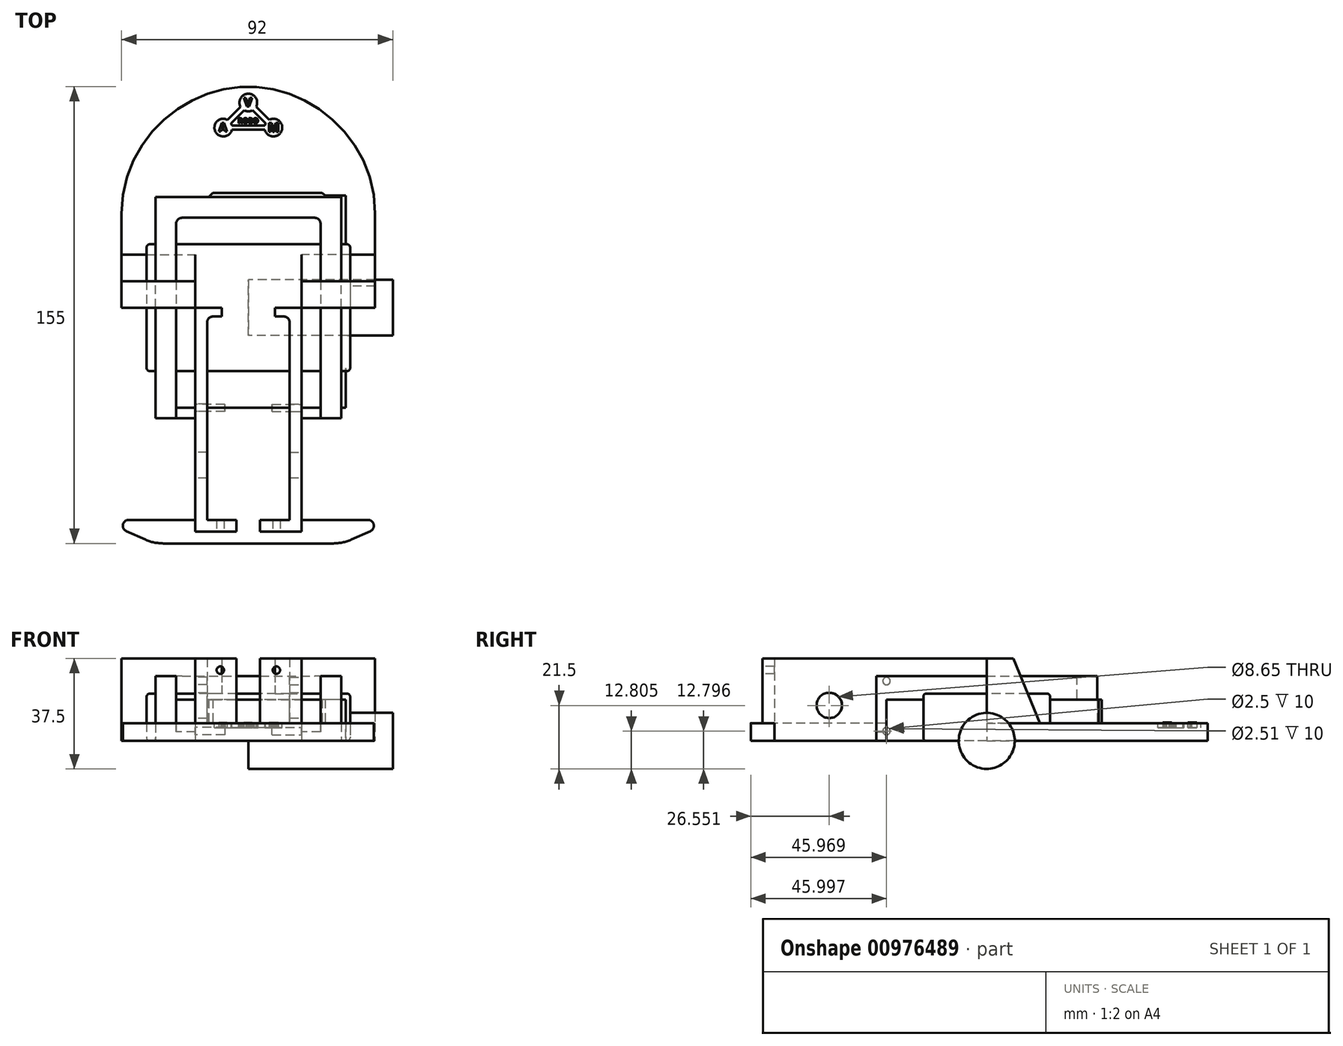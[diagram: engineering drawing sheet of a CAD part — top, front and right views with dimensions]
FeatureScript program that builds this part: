
annotation { "Feature Type Name" : "Feature", "Feature Type Description" : "" }
export const myFeature = defineFeature(function(context is Context, id is Id, definition is map)
    precondition{}
    {
        {
            var Q0;
            Q0=qCreatedBy(makeId("Top.planeOp"),FACE);
            var sketch = newSketch(context, id + "F0", { "sketchPlane" : qUnion([Q0])});
            skLineSegment(sketch, "E0.bottom", {"start": v(34.5, 21.5) * mm, "end": v(-34.5, 21.5) * mm});
            skLineSegment(sketch, "E0.top", {"start": v(34.5, -21.5) * mm, "end": v(-34.5, -21.5) * mm});
            skLineSegment(sketch, "E0.left", {"start": v(34.5, 21.5) * mm, "end": v(34.5, -21.5) * mm});
            skLineSegment(sketch, "E0.right", {"start": v(-34.5, 21.5) * mm, "end": v(-34.5, -21.5) * mm});
            skPoint(sketch, "E0.middle", {"position": v(0, 0) * mm});
            skSolve(sketch);
        }
        {
            var Q0;
            Q0 = qSketchRegion(id + "F0", true);
            extrude(context, id + "F1", {"entities" : qUnion([Q0]), "depth" : 16 * mm, "offsetDistance" : 25 * mm});
        }
        {
            var Q0;
            Q0=makeQuery(id+"F1.opExtrude","SWEPT_EDGE",EDGE,{"disambiguationData":[OSD([sQuery(id+"F0.wireOp",EDGE,"E0.bottom"),sQuery(id+"F0.wireOp",EDGE,"E0.right")])]});
            var Q1;
            Q1=makeQuery(id+"F1.opExtrude","SWEPT_EDGE",EDGE,{"disambiguationData":[OSD([sQuery(id+"F0.wireOp",EDGE,"E0.top"),sQuery(id+"F0.wireOp",EDGE,"E0.left")])]});
            var Q2;
            Q2=makeQuery(id+"F1.opExtrude","SWEPT_EDGE",EDGE,{"disambiguationData":[OSD([sQuery(id+"F0.wireOp",EDGE,"E0.top"),sQuery(id+"F0.wireOp",EDGE,"E0.right")])]});
            var Q3;
            Q3=makeQuery(id+"F1.opExtrude","CAP_EDGE",EDGE,{"disambiguationData":[OSD([sQuery(id+"F0.wireOp",EDGE,"E0.top")])],"isStart":true});
            var Q4;
            Q4=makeQuery(id+"F1.opExtrude","CAP_EDGE",EDGE,{"disambiguationData":[OSD([sQuery(id+"F0.wireOp",EDGE,"E0.left")])],"isStart":false});
            var Q5;
            Q5=makeQuery(id+"F1.opExtrude","CAP_EDGE",EDGE,{"disambiguationData":[OSD([sQuery(id+"F0.wireOp",EDGE,"E0.right")])],"isStart":true});
            var Q6;
            Q6=makeQuery(id+"F1.opExtrude","CAP_EDGE",EDGE,{"disambiguationData":[OSD([sQuery(id+"F0.wireOp",EDGE,"E0.right")])],"isStart":false});
            var Q7;
            Q7=makeQuery(id+"F1.opExtrude","SWEPT_EDGE",EDGE,{"disambiguationData":[OSD([sQuery(id+"F0.wireOp",EDGE,"E0.bottom"),sQuery(id+"F0.wireOp",EDGE,"E0.left")])]});
            var Q8;
            Q8=makeQuery(id+"F1.opExtrude","CAP_EDGE",EDGE,{"disambiguationData":[OSD([sQuery(id+"F0.wireOp",EDGE,"E0.bottom")])],"isStart":true});
            var Q9;
            Q9=makeQuery(id+"F1.opExtrude","CAP_EDGE",EDGE,{"disambiguationData":[OSD([sQuery(id+"F0.wireOp",EDGE,"E0.bottom")])],"isStart":false});
            var Q10;
            Q10=makeQuery(id+"F1.opExtrude","CAP_EDGE",EDGE,{"disambiguationData":[OSD([sQuery(id+"F0.wireOp",EDGE,"E0.top")])],"isStart":false});
            var Q11;
            Q11=makeQuery(id+"F1.opExtrude","CAP_EDGE",EDGE,{"disambiguationData":[OSD([sQuery(id+"F0.wireOp",EDGE,"E0.left")])],"isStart":true});
            fillet(context, id + "F2", {"entities" : qUnion([Q0, Q1, Q2, Q3, Q4, Q5, Q6, Q7, Q8, Q9, Q10, Q11]), "radius" : 1 * mm, "tangentPropagation" : true, "allowEdgeOverflow" : false});
        }
        {
            var Q0;
            Q0=qCreatedBy(makeId("Right.planeOp"),FACE);
            var sketch = newSketch(context, id + "F3", { "sketchPlane" : qUnion([Q0])});
            skCircle(sketch, "E1", {"center": v(0, 0) * mm, "radius": 9.5 * mm});
            skSolve(sketch);
        }
        {
            var Q0;
            Q0 = qSketchRegion(id + "F3", true);
            extrude(context, id + "F4", {"entities" : qUnion([Q0]), "depth" : 49 * mm, "offsetDistance" : 25 * mm});
        }
        {
            var Q0;
            Q0=qCreatedBy(makeId("Top.planeOp"),FACE);
            var sketch = newSketch(context, id + "F5", { "sketchPlane" : qUnion([Q0])});
            skLineSegment(sketch, "E2", {"start": v(33, 38) * mm, "end": v(33, -34) * mm});
            skLineSegment(sketch, "E3", {"start": v(33, -34) * mm, "end": v(-30, -34) * mm});
            skLineSegment(sketch, "E4", {"start": v(-30, -34) * mm, "end": v(-30, 34) * mm});
            skLineSegment(sketch, "E5", {"start": v(-30, 34) * mm, "end": v(-27.12, 36.88) * mm});
            skLineSegment(sketch, "E6", {"start": v(-27.12, 36.88) * mm, "end": v(-14.12, 36.88) * mm});
            skLineSegment(sketch, "E7", {"start": v(-14.12, 36.88) * mm, "end": v(-12, 39) * mm});
            skLineSegment(sketch, "E8", {"start": v(-12, 39) * mm, "end": v(25, 39) * mm});
            skLineSegment(sketch, "E9", {"start": v(33, 38) * mm, "end": v(26, 38) * mm});
            skLineSegment(sketch, "E10", {"start": v(26, 38) * mm, "end": v(25, 39) * mm});
            skLineSegment(sketch, "E11", {"start": v(-30, 0) * mm, "end": v(0, 0) * mm, "construction": true});
            skSolve(sketch);
        }
        {
            var Q0;
            Q0 = qSketchRegion(id + "F5", true);
            extrude(context, id + "F6", {"entities" : qUnion([Q0]), "depth" : 14 * mm, "offsetDistance" : 25 * mm});
        }
        {
            var Q0;
            Q0=qCreatedBy(makeId("Top.planeOp"),FACE);
            var sketch = newSketch(context, id + "F7", { "sketchPlane" : qUnion([Q0])});
            skLineSegment(sketch, "E12", {"start": v(-18, -72) * mm, "end": v(-18, 0) * mm});
            skLineSegment(sketch, "E13", {"start": v(-18, 0) * mm, "end": v(-43, 0) * mm});
            skLineSegment(sketch, "E14", {"start": v(-43, 0) * mm, "end": v(-43, 32) * mm});
            skLineSegment(sketch, "E15", {"start": v(-43, 32) * mm, "end": v(-43, 57) * mm, "construction": true});
            skLineSegment(sketch, "E16", {"start": v(-18, -72) * mm, "end": v(-40.58, -72) * mm});
            skLineSegment(sketch, "E17", {"start": v(0, -80) * mm, "end": v(-28.82, -80) * mm});
            skLineSegment(sketch, "E18", {"start": v(-18, 0) * mm, "end": v(0, 0) * mm, "construction": true});
            skLineSegment(sketch, "E19", {"start": v(0, 0) * mm, "end": v(0, -80) * mm, "construction": true});
            skLineSegment(sketch, "E20", {"start": v(-41.39, -75.83) * mm, "end": v(-34.9, -78.7) * mm});
            skPoint(sketch, "E21.visualSharp", {"position": v(-50, -72) * mm});
            skArc(sketch, "E21.filletArc", {"start": v(-40.58, -72) * mm, "mid": v(-42.53, -73.58) * mm, "end": v(-41.39, -75.83) * mm});
            skLineSegment(sketch, "E22", {"start": v(0, 0) * mm, "end": v(0, 75) * mm, "construction": true});
            skArc(sketch, "E23.MirrorCS", {"start": v(40.58, -72) * mm, "mid": v(42.53, -73.58) * mm, "end": v(41.39, -75.83) * mm});
            skLineSegment(sketch, "E24.MirrorCS", {"start": v(41.39, -75.83) * mm, "end": v(34.9, -78.7) * mm});
            skLineSegment(sketch, "E25.MirrorCS", {"start": v(18, -72) * mm, "end": v(40.58, -72) * mm});
            skLineSegment(sketch, "E26.MirrorCS", {"start": v(18, 0) * mm, "end": v(43, 0) * mm});
            skLineSegment(sketch, "E27.MirrorCS", {"start": v(18, 0) * mm, "end": v(0, 0) * mm, "construction": true});
            skLineSegment(sketch, "E28.MirrorCS", {"start": v(43, 32) * mm, "end": v(43, 57) * mm, "construction": true});
            skLineSegment(sketch, "E29.MirrorCS", {"start": v(0, -80) * mm, "end": v(28.82, -80) * mm});
            skPoint(sketch, "E30.MirrorP", {"position": v(50, -72) * mm});
            skLineSegment(sketch, "E31.MirrorCS", {"start": v(18, -72) * mm, "end": v(18, 0) * mm});
            skLineSegment(sketch, "E32.MirrorCS", {"start": v(43, 0) * mm, "end": v(43, 32) * mm});
            skFitSpline(sketch, "E33", {"points": [v(-43, 32) * mm, v(0, 75) * mm, v(43, 32) * mm], "startDerivative": vector(0, 150) * mm, "endDerivative": vector(0, -150) * mm});
            skPoint(sketch, "E34.visualSharp", {"position": v(-32, -80) * mm});
            skArc(sketch, "E34.filletArc", {"start": v(-34.9, -78.7) * mm, "mid": v(-31.93, -79.67) * mm, "end": v(-28.82, -80) * mm});
            skPoint(sketch, "E35.visualSharp", {"position": v(32, -80) * mm});
            skArc(sketch, "E35.filletArc", {"start": v(28.82, -80) * mm, "mid": v(31.93, -79.67) * mm, "end": v(34.9, -78.7) * mm});
            skSolve(sketch);
        }
        {
            var Q0;
            Q0 = qSketchRegion(id + "F7", true);
            extrude(context, id + "F8", {"entities" : qUnion([Q0]), "depth" : 6 * mm, "offsetDistance" : 25 * mm});
        }
        {
            var Q0;
            Q0=makeQuery(id+"F8.opExtrude","CAP_FACE",FACE,{"disambiguationData":[OSD([sQuery(id+"F7.wireOp",EDGE,"E12"),sQuery(id+"F7.wireOp",EDGE,"E13"),sQuery(id+"F7.wireOp",EDGE,"E14"),sQuery(id+"F7.wireOp",EDGE,"E16"),sQuery(id+"F7.wireOp",EDGE,"E17"),sQuery(id+"F7.wireOp",EDGE,"E20"),sQuery(id+"F7.wireOp",EDGE,"E21.filletArc"),sQuery(id+"F7.wireOp",EDGE,"E23.MirrorCS"),sQuery(id+"F7.wireOp",EDGE,"E24.MirrorCS"),sQuery(id+"F7.wireOp",EDGE,"E25.MirrorCS"),sQuery(id+"F7.wireOp",EDGE,"E26.MirrorCS"),sQuery(id+"F7.wireOp",EDGE,"E29.MirrorCS"),sQuery(id+"F7.wireOp",EDGE,"E31.MirrorCS"),sQuery(id+"F7.wireOp",EDGE,"E32.MirrorCS"),sQuery(id+"F7.wireOp",EDGE,"E33")])],"isStart":false});
            var sketch = newSketch(context, id + "F9", { "sketchPlane" : qUnion([Q0])});
            skLineSegment(sketch, "E36.bottom", {"start": v(-18, 0) * mm, "end": v(-14, 0) * mm});
            skLineSegment(sketch, "E36.top", {"start": v(-18, -72) * mm, "end": v(-14, -72) * mm});
            skLineSegment(sketch, "E36.left", {"start": v(-18, 0) * mm, "end": v(-18, -72) * mm});
            skLineSegment(sketch, "E36.right", {"start": v(-14, 0) * mm, "end": v(-14, -72) * mm});
            skLineSegment(sketch, "E37", {"start": v(0, 0) * mm, "end": v(0, -62.9) * mm, "construction": true});
            skPoint(sketch, "E37.endSnap0", {"position": v(0, -80) * mm});
            skLineSegment(sketch, "E38.MirrorCS", {"start": v(18, -72) * mm, "end": v(14, -72) * mm});
            skLineSegment(sketch, "E39.MirrorCS", {"start": v(18, 0) * mm, "end": v(14, 0) * mm});
            skLineSegment(sketch, "E40.MirrorCS", {"start": v(18, 0) * mm, "end": v(18, -72) * mm});
            skLineSegment(sketch, "E41.MirrorCS", {"start": v(14, 0) * mm, "end": v(14, -72) * mm});
            skLineSegment(sketch, "E42.bottom", {"start": v(-14, 0) * mm, "end": v(-9, 0) * mm});
            skLineSegment(sketch, "E42.top", {"start": v(-14, -3) * mm, "end": v(-9, -3) * mm});
            skLineSegment(sketch, "E42.left", {"start": v(-14, 0) * mm, "end": v(-14, -3) * mm});
            skLineSegment(sketch, "E42.right", {"start": v(-9, 0) * mm, "end": v(-9, -3) * mm});
            skLineSegment(sketch, "E43.bottom", {"start": v(14, 0) * mm, "end": v(9, 0) * mm});
            skLineSegment(sketch, "E43.top", {"start": v(14, -3) * mm, "end": v(9, -3) * mm});
            skLineSegment(sketch, "E43.left", {"start": v(14, 0) * mm, "end": v(14, -3) * mm});
            skLineSegment(sketch, "E43.right", {"start": v(9, 0) * mm, "end": v(9, -3) * mm});
            skSolve(sketch);
        }
        {
            var Q0;
            {var subQ0=sQuery(id+"F9.wireOp",EDGE,"E42.bottom");var subQ2=sQuery(id+"F9.wireOp",EDGE,"E36.bottom");var subQ7=sQuery(id+"F9.wireOp",EDGE,"E43.bottom");var subQ13=sQuery(id+"F9.wireOp",EDGE,"E38.MirrorCS");Q0=qUnion([makeQuery(id+"F9.imprint","IMPRINT",FACE,{"disambiguationData":[TD([[makeQuery(id+"F9.imprint","IMPRINT",EDGE,{"derivedFrom":subQ13}),-1.0]])]}),makeQuery(id+"F9.imprint","IMPRINT",FACE,{"disambiguationData":[TD([[makeQuery(id+"F9.imprint","IMPRINT",EDGE,{"derivedFrom":subQ7}),1.0]])]}),makeQuery(id+"F9.imprint","IMPRINT",FACE,{"disambiguationData":[TD([[makeQuery(id+"F9.imprint","IMPRINT",EDGE,{"derivedFrom":subQ2}),-1.0]])]}),makeQuery(id+"F9.imprint","IMPRINT",FACE,{"disambiguationData":[TD([[makeQuery(id+"F9.imprint","IMPRINT",EDGE,{"derivedFrom":subQ0}),-1.0]])]})]);}
            extrude(context, id + "F10", {"entities" : qUnion([Q0]), "operationType" : NewBodyOperationType.ADD, "depth" : 22 * mm, "offsetDistance" : 25 * mm});
        }
        {
            var Q0;
            Q0=makeQuery(id+"F10.opExtrude","SWEPT_FACE",FACE,{"disambiguationData":[OSD([sQuery(id+"F9.wireOp",EDGE,"E38.MirrorCS")])]});
            var sketch = newSketch(context, id + "F11", { "sketchPlane" : qUnion([Q0])});
            skLineSegment(sketch, "E44", {"start": v(0, 0) * mm, "end": v(0, 48) * mm, "construction": true});
            skLineSegment(sketch, "E45.bottom", {"start": v(18, 28) * mm, "end": v(4, 28) * mm});
            skLineSegment(sketch, "E45.top", {"start": v(18, 6) * mm, "end": v(4, 6) * mm});
            skLineSegment(sketch, "E45.left", {"start": v(18, 28) * mm, "end": v(18, 6) * mm});
            skLineSegment(sketch, "E45.right", {"start": v(4, 28) * mm, "end": v(4, 6) * mm});
            skLineSegment(sketch, "E46.MirrorCS", {"start": v(-18, 6) * mm, "end": v(-4, 6) * mm});
            skLineSegment(sketch, "E47.MirrorCS", {"start": v(-4, 28) * mm, "end": v(-4, 6) * mm});
            skLineSegment(sketch, "E48.MirrorCS", {"start": v(-18, 28) * mm, "end": v(-18, 6) * mm});
            skLineSegment(sketch, "E49.MirrorCS", {"start": v(-18, 28) * mm, "end": v(-4, 28) * mm});
            skSolve(sketch);
        }
        {
            var Q0;
            Q0 = qSketchRegion(id + "F11", true);
            extrude(context, id + "F12", {"entities" : qUnion([Q0]), "operationType" : NewBodyOperationType.ADD, "depth" : 4 * mm, "offsetDistance" : 25 * mm});
        }
        {
            var Q0;
            Q0=qCreatedBy(makeId("Top.planeOp"),FACE);
            var sketch = newSketch(context, id + "F13", { "sketchPlane" : qUnion([Q0])});
            skLineSegment(sketch, "E50.bottom", {"start": v(-31.5, -37.5) * mm, "end": v(31.5, -37.5) * mm});
            skLineSegment(sketch, "E50.top", {"start": v(-31.5, 37.5) * mm, "end": v(31.5, 37.5) * mm});
            skLineSegment(sketch, "E50.left", {"start": v(-31.5, -37.5) * mm, "end": v(-31.5, 37.5) * mm});
            skLineSegment(sketch, "E50.right", {"start": v(31.5, -37.5) * mm, "end": v(31.5, 37.5) * mm});
            skPoint(sketch, "E50.middle", {"position": v(0, 0) * mm});
            skLineSegment(sketch, "E51", {"start": v(0, 0) * mm, "end": v(0, 37.5) * mm, "construction": true});
            skSolve(sketch);
        }
        {
            var Q0;
            Q0=makeQuery(id+"F13.imprint","IMPRINT",FACE,{"disambiguationData":[TD([[makeQuery(id+"F13.imprint","IMPRINT",EDGE,{"derivedFrom":sQuery(id+"F13.wireOp",EDGE,"E50.bottom")}),1.0]])]});
            extrude(context, id + "F14", {"entities" : qUnion([Q0]), "depth" : 3 * mm, "offsetDistance" : 25 * mm});
        }
        {
            var Q0;
            Q0=makeQuery(id+"F14.opExtrude","CAP_FACE",FACE,{"disambiguationData":[OSD([sQuery(id+"F13.wireOp",EDGE,"E50.bottom"),sQuery(id+"F13.wireOp",EDGE,"E50.top"),sQuery(id+"F13.wireOp",EDGE,"E50.left"),sQuery(id+"F13.wireOp",EDGE,"E50.right")])],"isStart":false});
            var sketch = newSketch(context, id + "F15", { "sketchPlane" : qUnion([Q0])});
            skLineSegment(sketch, "E52", {"start": v(0, 0) * mm, "end": v(0, -40) * mm, "construction": true});
            skPoint(sketch, "E52.endSnap0", {"position": v(0, -37.5) * mm});
            skLineSegment(sketch, "E53.bottom", {"start": v(-31.5, 37.5) * mm, "end": v(-24.5, 37.5) * mm});
            skLineSegment(sketch, "E53.top", {"start": v(-31.5, -37.5) * mm, "end": v(-24.5, -37.5) * mm});
            skLineSegment(sketch, "E53.left", {"start": v(-31.5, 37.5) * mm, "end": v(-31.5, -37.5) * mm});
            skLineSegment(sketch, "E53.right", {"start": v(-24.5, 37.5) * mm, "end": v(-24.5, -37.5) * mm});
            skLineSegment(sketch, "E54.MirrorCS", {"start": v(31.5, -37.5) * mm, "end": v(24.5, -37.5) * mm});
            skLineSegment(sketch, "E55.MirrorCS", {"start": v(31.5, 37.5) * mm, "end": v(24.5, 37.5) * mm});
            skLineSegment(sketch, "E56.MirrorCS", {"start": v(31.5, 37.5) * mm, "end": v(31.5, -37.5) * mm});
            skLineSegment(sketch, "E57.MirrorCS", {"start": v(24.5, 37.5) * mm, "end": v(24.5, -37.5) * mm});
            skLineSegment(sketch, "E58.bottom", {"start": v(-24.5, 37.5) * mm, "end": v(24.5, 37.5) * mm});
            skLineSegment(sketch, "E58.top", {"start": v(-24.5, 30.5) * mm, "end": v(24.5, 30.5) * mm});
            skLineSegment(sketch, "E58.left", {"start": v(-24.5, 37.5) * mm, "end": v(-24.5, 30.5) * mm});
            skLineSegment(sketch, "E58.right", {"start": v(24.5, 37.5) * mm, "end": v(24.5, 30.5) * mm});
            skSolve(sketch);
        }
        {
            var Q0;
            {var subQ0=sQuery(id+"F15.wireOp",EDGE,"E58.bottom");var subQ2=sQuery(id+"F15.wireOp",EDGE,"E53.bottom");var subQ10=sQuery(id+"F15.wireOp",EDGE,"E54.MirrorCS");Q0=qUnion([makeQuery(id+"F15.imprint","IMPRINT",FACE,{"disambiguationData":[TD([[makeQuery(id+"F15.imprint","IMPRINT",EDGE,{"derivedFrom":subQ2}),-1.0]])]}),makeQuery(id+"F15.imprint","IMPRINT",FACE,{"disambiguationData":[TD([[makeQuery(id+"F15.imprint","IMPRINT",EDGE,{"derivedFrom":subQ10}),1.0]])]}),makeQuery(id+"F15.imprint","IMPRINT",FACE,{"disambiguationData":[TD([[makeQuery(id+"F15.imprint","IMPRINT",EDGE,{"derivedFrom":subQ0}),-1.0]])]})]);}
            extrude(context, id + "F16", {"entities" : qUnion([Q0]), "operationType" : NewBodyOperationType.ADD, "depth" : 19 * mm, "offsetDistance" : 25 * mm});
        }
        {
            var Q0;
            Q0=makeQuery(id+"F12.boolean.opBoolean","MERGE",FACE,{"derivedFrom":[makeQuery(id+"F10.boolean.opBoolean","MERGE",FACE,{"derivedFrom":[makeQuery(id+"F8.opExtrude","SWEPT_FACE",FACE,{"disambiguationData":[OSD([sQuery(id+"F7.wireOp",EDGE,"E12")])]}),makeQuery(id+"F10.opExtrude","SWEPT_FACE",FACE,{"disambiguationData":[OSD([sQuery(id+"F9.wireOp",EDGE,"E36.left")])]})]}),makeQuery(id+"F12.opExtrude","SWEPT_FACE",FACE,{"disambiguationData":[OSD([sQuery(id+"F11.wireOp",EDGE,"E48.MirrorCS")])]})]});
            var sketch = newSketch(context, id + "F17", { "sketchPlane" : qUnion([Q0])});
            skLineSegment(sketch, "E59", {"start": v(0, 6) * mm, "end": v(0, 28) * mm});
            skLineSegment(sketch, "E60", {"start": v(0, 28) * mm, "end": v(-9, 28) * mm});
            skLineSegment(sketch, "E61", {"start": v(-9, 28) * mm, "end": v(-18, 6) * mm});
            skLineSegment(sketch, "E62", {"start": v(-18, 6) * mm, "end": v(0, 6) * mm});
            skSolve(sketch);
        }
        {
            var Q0;
            Q0 = qSketchRegion(id + "F17", true);
            extrude(context, id + "F18", {"entities" : qUnion([Q0]), "depth" : 25 * mm, "offsetDistance" : 25 * mm});
        }
        {
            var Q0;
            Q0=makeQuery(id+"F12.boolean.opBoolean","MERGE",FACE,{"derivedFrom":[makeQuery(id+"F10.boolean.opBoolean","MERGE",FACE,{"derivedFrom":[makeQuery(id+"F8.opExtrude","SWEPT_FACE",FACE,{"disambiguationData":[OSD([sQuery(id+"F7.wireOp",EDGE,"E31.MirrorCS")])]}),makeQuery(id+"F10.opExtrude","SWEPT_FACE",FACE,{"disambiguationData":[OSD([sQuery(id+"F9.wireOp",EDGE,"E40.MirrorCS")])]})]}),makeQuery(id+"F12.opExtrude","SWEPT_FACE",FACE,{"disambiguationData":[OSD([sQuery(id+"F11.wireOp",EDGE,"E45.left")])]})]});
            var sketch = newSketch(context, id + "F19", { "sketchPlane" : qUnion([Q0])});
            skLineSegment(sketch, "E63", {"start": v(0, 28) * mm, "end": v(0, 6) * mm});
            skLineSegment(sketch, "E64", {"start": v(0, 6) * mm, "end": v(18, 6) * mm});
            skLineSegment(sketch, "E65", {"start": v(0, 28) * mm, "end": v(9, 28) * mm});
            skLineSegment(sketch, "E66", {"start": v(9, 28) * mm, "end": v(18, 6) * mm});
            skSolve(sketch);
        }
        {
            var Q0;
            Q0 = qSketchRegion(id + "F19", true);
            extrude(context, id + "F20", {"entities" : qUnion([Q0]), "depth" : 25 * mm, "offsetDistance" : 25 * mm});
        }
        {
            var Q0;
            Q0=makeQuery(id+"F12.boolean.opBoolean","MERGE",FACE,{"derivedFrom":[makeQuery(id+"F10.boolean.opBoolean","MERGE",FACE,{"derivedFrom":[makeQuery(id+"F8.opExtrude","SWEPT_FACE",FACE,{"disambiguationData":[OSD([sQuery(id+"F7.wireOp",EDGE,"E12")])]}),makeQuery(id+"F10.opExtrude","SWEPT_FACE",FACE,{"disambiguationData":[OSD([sQuery(id+"F9.wireOp",EDGE,"E36.left")])]})]}),makeQuery(id+"F12.opExtrude","SWEPT_FACE",FACE,{"disambiguationData":[OSD([sQuery(id+"F11.wireOp",EDGE,"E48.MirrorCS")])]})]});
            var sketch = newSketch(context, id + "F21", { "sketchPlane" : qUnion([Q0])});
            skCircle(sketch, "E67", {"center": v(34, 20.31) * mm, "radius": 1.25 * mm});
            skLineSegment(sketch, "E68", {"start": v(34, 20.31) * mm, "end": v(34, 28) * mm, "construction": true});
            skLineSegment(sketch, "E69", {"start": v(34, 20.31) * mm, "end": v(0, 20.31) * mm, "construction": true});
            skCircle(sketch, "E70", {"center": v(34, 3.3) * mm, "radius": 1.25 * mm});
            skLineSegment(sketch, "E71", {"start": v(34, 3.3) * mm, "end": v(34, 0) * mm});
            skLineSegment(sketch, "E72", {"start": v(34, 0) * mm, "end": v(34, 3.3) * mm, "construction": true});
            skLineSegment(sketch, "E73", {"start": v(0, 3.3) * mm, "end": v(34, 3.3) * mm, "construction": true});
            skCircle(sketch, "E74", {"center": v(53.45, 12) * mm, "radius": 4.33 * mm});
            skLineSegment(sketch, "E75", {"start": v(53.45, 12) * mm, "end": v(53.45, 28) * mm, "construction": true});
            skLineSegment(sketch, "E76", {"start": v(53.45, 12) * mm, "end": v(76, 12) * mm, "construction": true});
            skSolve(sketch);
        }
        {
            var Q0;
            Q0 = qSketchRegion(id + "F21", true);
            extrude(context, id + "F22", {"entities" : qUnion([Q0]), "operationType" : NewBodyOperationType.REMOVE, "oppositeDirection" : true, "depth" : 10 * mm, "offsetDistance" : 25 * mm});
        }
        {
            var Q0;
            Q0=makeQuery(id+"F12.boolean.opBoolean","MERGE",FACE,{"derivedFrom":[makeQuery(id+"F10.boolean.opBoolean","MERGE",FACE,{"derivedFrom":[makeQuery(id+"F8.opExtrude","SWEPT_FACE",FACE,{"disambiguationData":[OSD([sQuery(id+"F7.wireOp",EDGE,"E31.MirrorCS")])]}),makeQuery(id+"F10.opExtrude","SWEPT_FACE",FACE,{"disambiguationData":[OSD([sQuery(id+"F9.wireOp",EDGE,"E40.MirrorCS")])]})]}),makeQuery(id+"F12.opExtrude","SWEPT_FACE",FACE,{"disambiguationData":[OSD([sQuery(id+"F11.wireOp",EDGE,"E45.left")])]})]});
            var sketch = newSketch(context, id + "F23", { "sketchPlane" : qUnion([Q0])});
            skCircle(sketch, "E77", {"center": v(-53.4, 12.04) * mm, "radius": 4.3 * mm});
            skCircle(sketch, "E78", {"center": v(-34.03, 3.3) * mm, "radius": 1.26 * mm});
            skCircle(sketch, "E79", {"center": v(-33.99, 20.29) * mm, "radius": 1.28 * mm});
            skLineSegment(sketch, "E80", {"start": v(-53.4, 12.04) * mm, "end": v(-53.4, 28) * mm, "construction": true});
            skLineSegment(sketch, "E81", {"start": v(-53.4, 12.04) * mm, "end": v(-76, 12.04) * mm, "construction": true});
            skLineSegment(sketch, "E82", {"start": v(-33.99, 20.29) * mm, "end": v(-33.99, 28) * mm, "construction": true});
            skLineSegment(sketch, "E83", {"start": v(-33.99, 20.29) * mm, "end": v(0, 20.29) * mm, "construction": true});
            skLineSegment(sketch, "E84", {"start": v(-34.03, 3.3) * mm, "end": v(0, 3.3) * mm, "construction": true});
            skLineSegment(sketch, "E85", {"start": v(-34.03, 3.3) * mm, "end": v(-34.03, 0) * mm, "construction": true});
            skSolve(sketch);
        }
        {
            var Q0;
            Q0 = qSketchRegion(id + "F23", true);
            extrude(context, id + "F24", {"entities" : qUnion([Q0]), "operationType" : NewBodyOperationType.REMOVE, "oppositeDirection" : true, "depth" : 10 * mm, "offsetDistance" : 25 * mm});
        }
        {
            var Q0;
            Q0=makeQuery(id+"F12.opExtrude","CAP_FACE",FACE,{"disambiguationData":[OSD([sQuery(id+"F11.wireOp",EDGE,"E46.MirrorCS"),sQuery(id+"F11.wireOp",EDGE,"E47.MirrorCS"),sQuery(id+"F11.wireOp",EDGE,"E48.MirrorCS"),sQuery(id+"F11.wireOp",EDGE,"E49.MirrorCS")])],"isStart":false});
            var sketch = newSketch(context, id + "F25", { "sketchPlane" : qUnion([Q0])});
            skLineSegment(sketch, "E86", {"start": v(0, 0) * mm, "end": v(0, 34.64) * mm, "construction": true});
            skLineSegment(sketch, "E87.bottom", {"start": v(0, 24) * mm, "end": v(-9.5, 24) * mm, "construction": true});
            skLineSegment(sketch, "E87.top", {"start": v(0, 0) * mm, "end": v(-9.5, 0) * mm});
            skLineSegment(sketch, "E87.left", {"start": v(0, 24) * mm, "end": v(0, 0) * mm});
            skLineSegment(sketch, "E87.right", {"start": v(-9.5, 24) * mm, "end": v(-9.5, 0) * mm, "construction": true});
            skLineSegment(sketch, "E88.MirrorCS", {"start": v(0, 24) * mm, "end": v(9.5, 24) * mm, "construction": true});
            skLineSegment(sketch, "E89.MirrorCS", {"start": v(9.5, 24) * mm, "end": v(9.5, 0) * mm, "construction": true});
            skLineSegment(sketch, "E90.MirrorCS", {"start": v(0, 0) * mm, "end": v(9.5, 0) * mm});
            skCircle(sketch, "E91", {"center": v(-9.5, 24) * mm, "radius": 1.25 * mm});
            skCircle(sketch, "E92", {"center": v(9.5, 24) * mm, "radius": 1.25 * mm});
            skSolve(sketch);
        }
        {
            var Q0;
            Q0 = qSketchRegion(id + "F25", true);
            extrude(context, id + "F26", {"entities" : qUnion([Q0]), "operationType" : NewBodyOperationType.REMOVE, "oppositeDirection" : true, "depth" : 5 * mm, "offsetDistance" : 25 * mm});
        }
        {
            var Q0;
            Q0=makeQuery(id+"F10.opExtrude","SWEPT_EDGE",EDGE,{"disambiguationData":[OSD([sQuery(id+"F9.wireOp",EDGE,"E36.top"),sQuery(id+"F9.wireOp",EDGE,"E36.right")])]});
            var Q1;
            Q1=makeQuery(id+"F10.opExtrude","SWEPT_EDGE",EDGE,{"disambiguationData":[OSD([sQuery(id+"F9.wireOp",EDGE,"E38.MirrorCS"),sQuery(id+"F9.wireOp",EDGE,"E41.MirrorCS")])]});
            var Q2;
            Q2=makeQuery(id+"F10.opExtrude","SWEPT_EDGE",EDGE,{"disambiguationData":[OSD([sQuery(id+"F9.wireOp",EDGE,"E36.right"),sQuery(id+"F9.wireOp",EDGE,"E42.top")])]});
            var Q3;
            Q3=makeQuery(id+"F10.opExtrude","SWEPT_EDGE",EDGE,{"disambiguationData":[OSD([sQuery(id+"F9.wireOp",EDGE,"E41.MirrorCS"),sQuery(id+"F9.wireOp",EDGE,"E43.top")])]});
            fillet(context, id + "F27", {"entities" : qUnion([Q0, Q1, Q2, Q3]), "radius" : 2 * mm, "tangentPropagation" : true, "allowEdgeOverflow" : false});
        }
        {
            var Q0;
            Q0=makeQuery(id+"F16.opExtrude","SWEPT_EDGE",EDGE,{"disambiguationData":[OSD([sQuery(id+"F15.wireOp",EDGE,"E53.right"),sQuery(id+"F15.wireOp",EDGE,"E58.top")])]});
            var Q1;
            Q1=makeQuery(id+"F16.opExtrude","SWEPT_EDGE",EDGE,{"disambiguationData":[OSD([sQuery(id+"F15.wireOp",EDGE,"E57.MirrorCS"),sQuery(id+"F15.wireOp",EDGE,"E58.top")])]});
            fillet(context, id + "F28", {"entities" : qUnion([Q0, Q1]), "radius" : 2 * mm, "tangentPropagation" : true, "allowEdgeOverflow" : false});
        }
        {
            var Q0;
            Q0=makeQuery(id+"F8.opExtrude","CAP_FACE",FACE,{"disambiguationData":[OSD([sQuery(id+"F7.wireOp",EDGE,"E12"),sQuery(id+"F7.wireOp",EDGE,"E13"),sQuery(id+"F7.wireOp",EDGE,"E14"),sQuery(id+"F7.wireOp",EDGE,"E16"),sQuery(id+"F7.wireOp",EDGE,"E17"),sQuery(id+"F7.wireOp",EDGE,"E20"),sQuery(id+"F7.wireOp",EDGE,"E21.filletArc"),sQuery(id+"F7.wireOp",EDGE,"E23.MirrorCS"),sQuery(id+"F7.wireOp",EDGE,"E24.MirrorCS"),sQuery(id+"F7.wireOp",EDGE,"E25.MirrorCS"),sQuery(id+"F7.wireOp",EDGE,"E26.MirrorCS"),sQuery(id+"F7.wireOp",EDGE,"E29.MirrorCS"),sQuery(id+"F7.wireOp",EDGE,"E31.MirrorCS"),sQuery(id+"F7.wireOp",EDGE,"E32.MirrorCS"),sQuery(id+"F7.wireOp",EDGE,"E33"),sQuery(id+"F7.wireOp",EDGE,"E34.filletArc"),sQuery(id+"F7.wireOp",EDGE,"E35.filletArc")])],"isStart":false});
            var sketch = newSketch(context, id + "F29", { "sketchPlane" : qUnion([Q0])});
            skLineSegment(sketch, "E93", {"start": v(0, 1.67) * mm, "end": v(0, 69.61) * mm, "construction": true});
            skCircle(sketch, "E94", {"center": v(0, 69.61) * mm, "radius": 3 * mm});
            skLineSegment(sketch, "E95", {"start": v(0, 69.61) * mm, "end": v(0, 75) * mm, "construction": true});
            skLineSegment(sketch, "E96", {"start": v(0, 61.1) * mm, "end": v(8.5, 61.1) * mm, "construction": true});
            skLineSegment(sketch, "E97", {"start": v(0, 61.1) * mm, "end": v(-8.5, 61.1) * mm, "construction": true});
            skCircle(sketch, "E98", {"center": v(8.5, 61.1) * mm, "radius": 3 * mm});
            skCircle(sketch, "E99", {"center": v(-8.5, 61.1) * mm, "radius": 3 * mm});
            skLineSegment(sketch, "E100", {"start": v(-9.75, 61.1) * mm, "end": v(-1.26, 69.59) * mm});
            skLineSegment(sketch, "E101", {"start": v(-7.25, 61.1) * mm, "end": v(1.24, 69.59) * mm});
            skLineSegment(sketch, "E102", {"start": v(-9.75, 61.1) * mm, "end": v(-7.25, 61.1) * mm});
            skLineSegment(sketch, "E103", {"start": v(-1.26, 69.59) * mm, "end": v(1.24, 69.59) * mm});
            skLineSegment(sketch, "E104.bottom", {"start": v(8.5, 61.85) * mm, "end": v(-8.5, 61.85) * mm});
            skLineSegment(sketch, "E104.top", {"start": v(8.5, 60.36) * mm, "end": v(-8.5, 60.36) * mm});
            skLineSegment(sketch, "E104.left", {"start": v(8.5, 61.85) * mm, "end": v(8.5, 60.36) * mm});
            skLineSegment(sketch, "E104.right", {"start": v(-8.5, 61.85) * mm, "end": v(-8.5, 60.36) * mm});
            skPoint(sketch, "E104.middle", {"position": v(0, 61.1) * mm});
            skLineSegment(sketch, "E105", {"start": v(9.75, 61.1) * mm, "end": v(7.25, 61.1) * mm});
            skLineSegment(sketch, "E106", {"start": v(9.75, 61.1) * mm, "end": v(1.26, 69.59) * mm});
            skLineSegment(sketch, "E107", {"start": v(7.25, 61.1) * mm, "end": v(-1.24, 69.59) * mm});
            skLineSegment(sketch, "E108", {"start": v(-1.24, 69.59) * mm, "end": v(1.26, 69.59) * mm});
            skText(sketch, "E109", { "text": "ROBO", "fontName": "OpenSans-Bold.ttf"});
            const initialGuessF29  = {"E109": [-0.0035, 0.0626, 1, 0, 0.0017]};
            skSetInitialGuess(sketch, initialGuessF29);
            skSolve(sketch);
        }
        {
            var Q0;
            Q0 = qSketchRegion(id + "F29", true);
            var Q1;
            {var subQ0=sQuery(id+"F29.wireOp",EDGE,"E108");var subQ1=sQuery(id+"F29.wireOp",EDGE,"E101");var subQ2=makeQuery(id+"F29.imprint","INTERSECT",VERTEX,{"derivedFrom":[subQ1,subQ0]});Q1=makeQuery(id+"F29.imprint","IMPRINT",FACE,{"disambiguationData":[TD([[makeQuery(id+"F29.imprint","IMPRINT",EDGE,{"disambiguationData":[TD([[subQ2,1.0]])],"derivedFrom":subQ1}),1.0]])]});}
            var Q2;
            {var subQ0=sQuery(id+"F29.wireOp",EDGE,"E101");var subQ1=sQuery(id+"F29.wireOp",EDGE,"E94");var subQ2=makeQuery(id+"F29.imprint","INTERSECT",VERTEX,{"derivedFrom":[subQ1,subQ0]});Q2=makeQuery(id+"F29.imprint","IMPRINT",FACE,{"disambiguationData":[TD([[makeQuery(id+"F29.imprint","IMPRINT",EDGE,{"disambiguationData":[TD([[subQ2,-1.0]])],"derivedFrom":subQ1}),1.0]])]});}
            var Q3;
            {var subQ0=sQuery(id+"F29.wireOp",EDGE,"E102");var subQ1=sQuery(id+"F29.wireOp",EDGE,"E101");var subQ2=makeQuery(id+"F29.imprint","INTERSECT",VERTEX,{"derivedFrom":[subQ1,subQ0]});Q3=makeQuery(id+"F29.imprint","IMPRINT",FACE,{"disambiguationData":[TD([[makeQuery(id+"F29.imprint","IMPRINT",EDGE,{"disambiguationData":[TD([[subQ2,-1.0]])],"derivedFrom":subQ1}),1.0]])]});}
            var Q4;
            {var subQ0=sQuery(id+"F29.wireOp",EDGE,"E104.left");var subQ1=sQuery(id+"F29.wireOp",EDGE,"E104.bottom");var subQ2=makeQuery(id+"F29.imprint","INTERSECT",VERTEX,{"derivedFrom":[subQ1,subQ0]});Q4=makeQuery(id+"F29.imprint","IMPRINT",FACE,{"disambiguationData":[TD([[makeQuery(id+"F29.imprint","IMPRINT",EDGE,{"disambiguationData":[TD([[subQ2,-1.0]])],"derivedFrom":subQ1}),1.0]])]});}
            var Q5;
            {var subQ0=sQuery(id+"F29.wireOp",EDGE,"E101");var subQ1=sQuery(id+"F29.wireOp",EDGE,"E99");var subQ2=makeQuery(id+"F29.imprint","INTERSECT",VERTEX,{"derivedFrom":[subQ1,subQ0]});Q5=makeQuery(id+"F29.imprint","IMPRINT",FACE,{"disambiguationData":[TD([[makeQuery(id+"F29.imprint","IMPRINT",EDGE,{"disambiguationData":[TD([[subQ2,1.0]])],"derivedFrom":subQ1}),1.0]])]});}
            var Q6;
            Q6=makeQuery(id+"F29.imprint","IMPRINT",FACE,{"disambiguationData":[TD([[makeQuery(id+"F29.imprint","IMPRINT",EDGE,{"derivedFrom":sQuery(id+"F29.wireOp",EDGE,"E109.sketch_text.stroke-0")}),-1.0]])]});
            var Q7;
            Q7=makeQuery(id+"F29.imprint","IMPRINT",FACE,{"disambiguationData":[TD([[makeQuery(id+"F29.imprint","IMPRINT",EDGE,{"derivedFrom":sQuery(id+"F29.wireOp",EDGE,"E109.sketch_text.stroke-19")}),-1.0]])]});
            var Q8;
            Q8=makeQuery(id+"F29.imprint","IMPRINT",FACE,{"disambiguationData":[TD([[makeQuery(id+"F29.imprint","IMPRINT",EDGE,{"derivedFrom":sQuery(id+"F29.wireOp",EDGE,"E109.sketch_text.stroke-33")}),-1.0]])]});
            var Q9;
            Q9=makeQuery(id+"F29.imprint","IMPRINT",FACE,{"disambiguationData":[TD([[makeQuery(id+"F29.imprint","IMPRINT",EDGE,{"derivedFrom":sQuery(id+"F29.wireOp",EDGE,"E109.sketch_text.stroke-58")}),-1.0]])]});
            var Q10;
            {var subQ0=sQuery(id+"F29.wireOp",EDGE,"E107");var subQ1=sQuery(id+"F29.wireOp",EDGE,"E98");var subQ2=makeQuery(id+"F29.imprint","INTERSECT",VERTEX,{"derivedFrom":[subQ1,subQ0]});Q10=makeQuery(id+"F29.imprint","IMPRINT",FACE,{"disambiguationData":[TD([[makeQuery(id+"F29.imprint","IMPRINT",EDGE,{"disambiguationData":[TD([[subQ2,-1.0]])],"derivedFrom":subQ1}),1.0]])]});}
            extrude(context, id + "F30", {"entities" : qUnion([Q0, Q1, Q2, Q3, Q4, Q5, Q6, Q7, Q8, Q9, Q10]), "operationType" : NewBodyOperationType.REMOVE, "oppositeDirection" : true, "depth" : 1.5 * mm, "offsetDistance" : 25 * mm});
        }
        {
            var Q0;
            Q0=makeQuery(id+"F30.boolean.opBoolean","COPY",FACE,{"derivedFrom":makeQuery(id+"F30.opExtrude","CAP_FACE",FACE,{"disambiguationData":[OSD([sQuery(id+"F29.wireOp",EDGE,"E94"),sQuery(id+"F29.wireOp",EDGE,"E98"),sQuery(id+"F29.wireOp",EDGE,"E99"),sQuery(id+"F29.wireOp",EDGE,"E100"),sQuery(id+"F29.wireOp",EDGE,"E101"),sQuery(id+"F29.wireOp",EDGE,"E104.bottom"),sQuery(id+"F29.wireOp",EDGE,"E104.top"),sQuery(id+"F29.wireOp",EDGE,"E106"),sQuery(id+"F29.wireOp",EDGE,"E107")])],"isStart":false})});
            var sketch = newSketch(context, id + "F31", { "sketchPlane" : qUnion([Q0])});
            skText(sketch, "E110", { "text": "V", "fontName": "OpenSans-Bold.ttf"});
            skText(sketch, "E111", { "text": "A", "fontName": "OpenSans-Bold.ttf"});
            skText(sketch, "E112", { "text": "M", "fontName": "OpenSans-Bold.ttf"});
            const initialGuessF31  = {"E110": [-0.00149, 0.06825, 1, 0, 0.003], "E111": [-0.01005, 0.05971, 1, 0, 0.003], "E112": [0.00661, 0.05968, 1, 0, 0.003]};
            skSetInitialGuess(sketch, initialGuessF31);
            skSolve(sketch);
        }
        {
            var Q0;
            Q0 = qSketchRegion(id + "F31", true);
            extrude(context, id + "F32", {"entities" : qUnion([Q0]), "operationType" : NewBodyOperationType.ADD, "depth" : 1.7 * mm, "offsetDistance" : 25 * mm});
        }
    });
